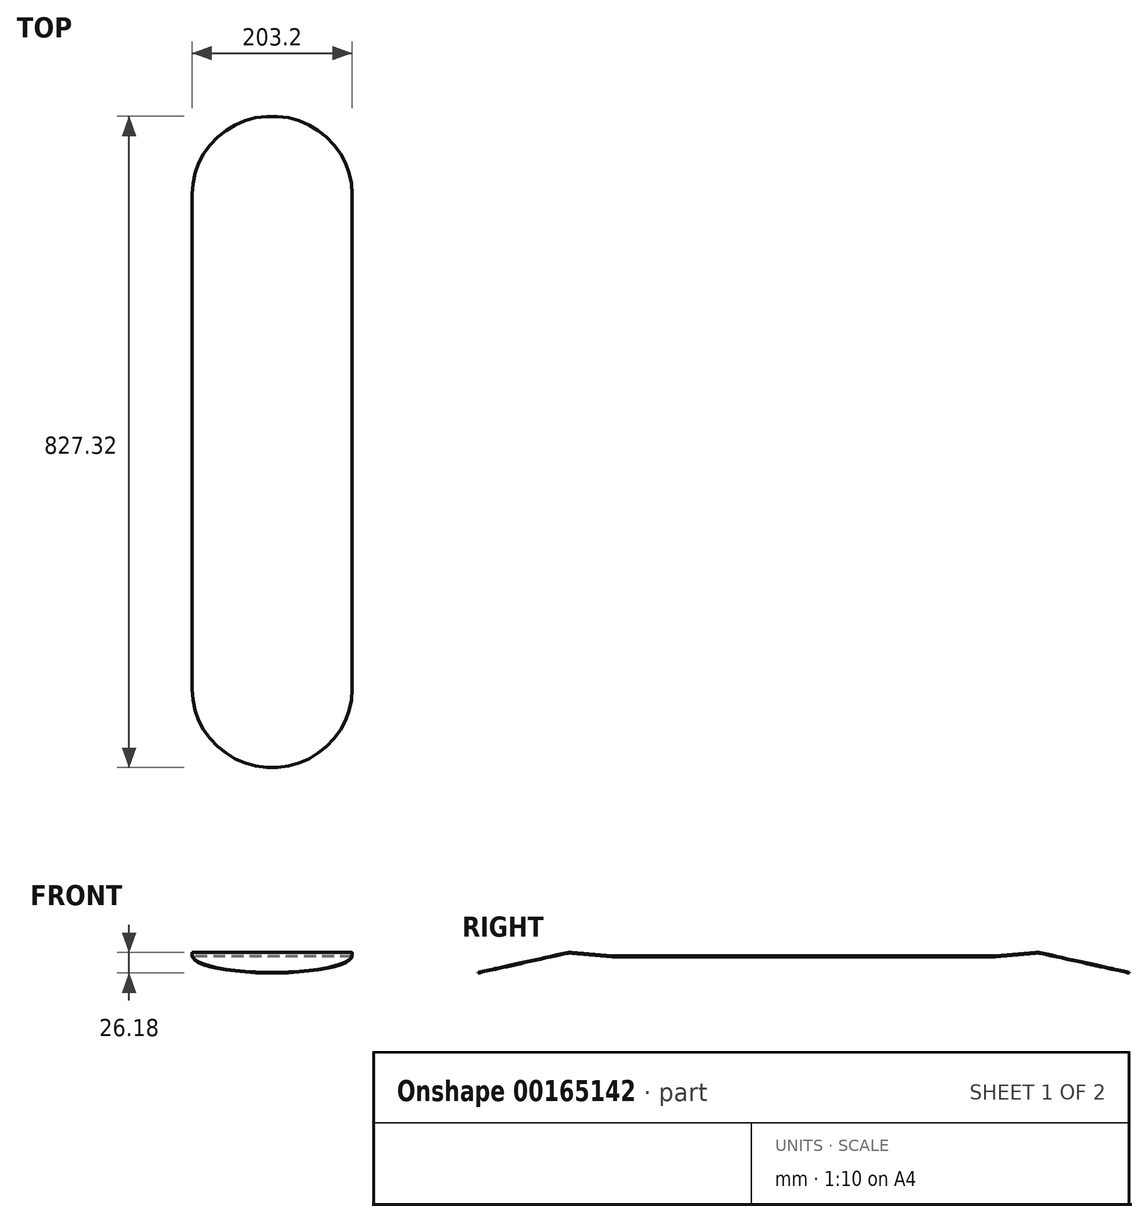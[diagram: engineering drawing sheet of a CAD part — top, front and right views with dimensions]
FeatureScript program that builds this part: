
annotation { "Feature Type Name" : "Feature", "Feature Type Description" : "" }
export const myFeature = defineFeature(function(context is Context, id is Id, definition is map)
    precondition{}
    {
        {
            var Q0;
            Q0=qCreatedBy(makeId("Top.planeOp"),FACE);
            var sketch = newSketch(context, id + "F0", { "sketchPlane" : qUnion([Q0])});
            skLineSegment(sketch, "E0.bottom", {"start": v(101.6, 241.3) * mm, "end": v(-101.6, 241.3) * mm});
            skLineSegment(sketch, "E0.top", {"start": v(101.6, -241.3) * mm, "end": v(-101.6, -241.3) * mm});
            skLineSegment(sketch, "E0.left", {"start": v(101.6, 241.3) * mm, "end": v(101.6, -241.3) * mm});
            skLineSegment(sketch, "E0.right", {"start": v(-101.6, 241.3) * mm, "end": v(-101.6, -241.3) * mm});
            skPoint(sketch, "E0.middle", {"position": v(0, 0) * mm});
            skSolve(sketch);
        }
        {
            var Q0;
            Q0=makeQuery(id+"F0.imprint","IMPRINT",FACE,{"disambiguationData":[TD([[makeQuery(id+"F0.imprint","IMPRINT",EDGE,{"derivedFrom":sQuery(id+"F0.wireOp",EDGE,"E0.bottom")}),1.0]])]});
            extrude(context, id + "F1", {"entities" : qUnion([Q0]), "depth" : 0.8 * mm});
        }
        {
            var Q0;
            Q0=makeQuery(id+"F1.opExtrude","SWEPT_FACE",FACE,{"disambiguationData":[OSD([sQuery(id+"F0.wireOp",EDGE,"E0.left")])]});
            var sketch = newSketch(context, id + "F2", { "sketchPlane" : qUnion([Q0])});
            skLineSegment(sketch, "E1", {"start": v(241.3, 0.8) * mm, "end": v(241.3, 0) * mm});
            skArc(sketch, "E2", {"start": v(241.3, 0) * mm, "mid": v(242.44, 0.02) * mm, "end": v(243.58, 0.1) * mm});
            skArc(sketch, "E3", {"start": v(241.3, 0.8) * mm, "mid": v(242.4, 0.82) * mm, "end": v(243.51, 0.9) * mm});
            skLineSegment(sketch, "E4", {"start": v(241.3, 0) * mm, "end": v(296.4, 0) * mm, "construction": true});
            skLineSegment(sketch, "E5.bottom", {"start": v(243.51, 0.9) * mm, "end": v(294.12, 5.32) * mm});
            skLineSegment(sketch, "E5.top", {"start": v(243.58, 0.1) * mm, "end": v(294.19, 4.53) * mm});
            skLineSegment(sketch, "E5.left", {"start": v(243.51, 0.9) * mm, "end": v(243.58, 0.1) * mm, "construction": true});
            skLineSegment(sketch, "E5.right", {"start": v(294.12, 5.32) * mm, "end": v(294.19, 4.53) * mm, "construction": true});
            skLineSegment(sketch, "E6", {"start": v(241.3, 26.2) * mm, "end": v(243.51, 0.9) * mm, "construction": true});
            skArc(sketch, "E7", {"start": v(301.9, 4.02) * mm, "mid": v(298.07, 4.57) * mm, "end": v(294.19, 4.53) * mm});
            skArc(sketch, "E8", {"start": v(302.08, 4.8) * mm, "mid": v(298.12, 5.36) * mm, "end": v(294.12, 5.32) * mm});
            skLineSegment(sketch, "E9.bottom", {"start": v(301.9, 4.02) * mm, "end": v(413.5, -20.76) * mm});
            skLineSegment(sketch, "E9.top", {"start": v(302.08, 4.8) * mm, "end": v(413.66, -19.98) * mm});
            skLineSegment(sketch, "E9.left", {"start": v(301.9, 4.02) * mm, "end": v(302.08, 4.8) * mm, "construction": true});
            skLineSegment(sketch, "E9.right", {"start": v(413.5, -20.76) * mm, "end": v(413.66, -19.98) * mm});
            skLineSegment(sketch, "E10", {"start": v(296.4, 5.42) * mm, "end": v(413.66, 5.42) * mm, "construction": true});
            skLineSegment(sketch, "E11", {"start": v(413.66, 5.42) * mm, "end": v(413.66, -19.98) * mm, "construction": true});
            skLineSegment(sketch, "E12", {"start": v(296.4, 0) * mm, "end": v(296.4, 5.42) * mm, "construction": true});
            skArc(sketch, "E13", {"start": v(-243.58, 0.1) * mm, "mid": v(-242.44, 0.02) * mm, "end": v(-241.3, 0) * mm});
            skArc(sketch, "E14", {"start": v(-243.51, 0.9) * mm, "mid": v(-242.4, 0.82) * mm, "end": v(-241.3, 0.8) * mm});
            skLineSegment(sketch, "E15", {"start": v(-241.3, 0) * mm, "end": v(-241.3, 0.8) * mm});
            skLineSegment(sketch, "E16.bottom", {"start": v(-243.58, 0.1) * mm, "end": v(-294.19, 4.53) * mm});
            skLineSegment(sketch, "E16.top", {"start": v(-243.51, 0.9) * mm, "end": v(-294.12, 5.32) * mm});
            skLineSegment(sketch, "E16.left", {"start": v(-243.58, 0.1) * mm, "end": v(-243.51, 0.9) * mm, "construction": true});
            skLineSegment(sketch, "E16.right", {"start": v(-294.19, 4.53) * mm, "end": v(-294.12, 5.32) * mm, "construction": true});
            skArc(sketch, "E17", {"start": v(-294.19, 4.53) * mm, "mid": v(-298.07, 4.57) * mm, "end": v(-301.9, 4.02) * mm});
            skArc(sketch, "E18", {"start": v(-294.12, 5.32) * mm, "mid": v(-298.12, 5.36) * mm, "end": v(-302.08, 4.8) * mm});
            skLineSegment(sketch, "E19.bottom", {"start": v(-301.9, 4.02) * mm, "end": v(-413.5, -20.76) * mm});
            skLineSegment(sketch, "E19.top", {"start": v(-302.08, 4.8) * mm, "end": v(-413.66, -19.98) * mm});
            skLineSegment(sketch, "E19.left", {"start": v(-301.9, 4.02) * mm, "end": v(-302.08, 4.8) * mm, "construction": true});
            skLineSegment(sketch, "E19.right", {"start": v(-413.5, -20.76) * mm, "end": v(-413.66, -19.98) * mm});
            skLineSegment(sketch, "E20", {"start": v(294.19, 4.53) * mm, "end": v(-294.19, 4.53) * mm, "construction": true});
            skLineSegment(sketch, "E21", {"start": v(0, 4.53) * mm, "end": v(0, 0.8) * mm, "construction": true});
            skLineSegment(sketch, "E22", {"start": v(413.5, -20.76) * mm, "end": v(-413.5, -20.76) * mm, "construction": true});
            skSolve(sketch);
        }
        {
            var Q0;
            Q0=makeQuery(id+"F2.imprint","IMPRINT",FACE,{"disambiguationData":[TD([[makeQuery(id+"F2.imprint","IMPRINT",EDGE,{"derivedFrom":sQuery(id+"F2.wireOp",EDGE,"E1")}),1.0]])]});
            var Q1;
            Q1=makeQuery(id+"F2.imprint","IMPRINT",FACE,{"disambiguationData":[TD([[makeQuery(id+"F2.imprint","IMPRINT",EDGE,{"derivedFrom":sQuery(id+"F2.wireOp",EDGE,"E13")}),1.0]])]});
            var Q2;
            Q2=makeQuery(id+"F1.opExtrude","SWEPT_FACE",FACE,{"disambiguationData":[OSD([sQuery(id+"F0.wireOp",EDGE,"E0.right")])]});
            extrude(context, id + "F3", {"entities" : qUnion([Q0, Q1]), "operationType" : NewBodyOperationType.ADD, "endBound" : BoundingType.UP_TO_SURFACE, "oppositeDirection" : true, "endBoundEntityFace" : qUnion([Q2]), "depth" : 25.4 * mm});
        }
        {
            var Q0;
            Q0=makeQuery(id+"F3.opExtrude","CAP_EDGE",EDGE,{"disambiguationData":[OSD([sQuery(id+"F2.wireOp",EDGE,"E9.right")])],"isStart":true});
            var Q1;
            Q1=makeQuery(id+"F3.opExtrude","CAP_EDGE",EDGE,{"disambiguationData":[OSD([sQuery(id+"F2.wireOp",EDGE,"E9.right")])],"isStart":false});
            var Q2;
            Q2=makeQuery(id+"F3.opExtrude","CAP_EDGE",EDGE,{"disambiguationData":[OSD([sQuery(id+"F2.wireOp",EDGE,"E19.right")])],"isStart":true});
            var Q3;
            Q3=makeQuery(id+"F3.opExtrude","CAP_EDGE",EDGE,{"disambiguationData":[OSD([sQuery(id+"F2.wireOp",EDGE,"E19.right")])],"isStart":false});
            fillet(context, id + "F4", {"entities" : qUnion([Q0, Q1, Q2, Q3]), "radius" : 101.6 * mm, "tangentPropagation" : true, "allowEdgeOverflow" : false});
        }
    });
